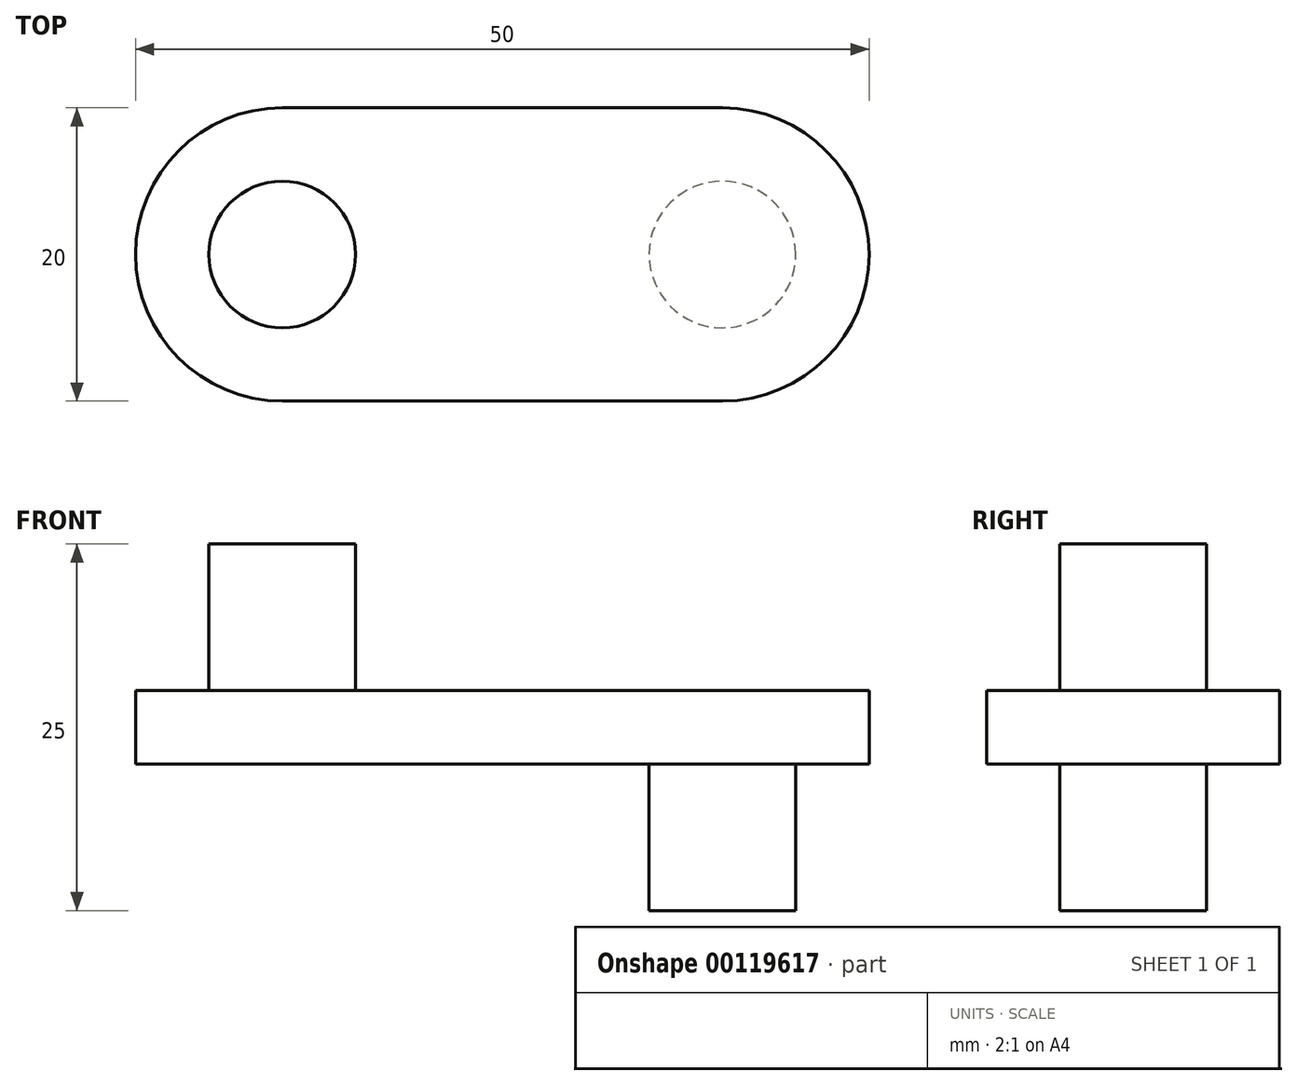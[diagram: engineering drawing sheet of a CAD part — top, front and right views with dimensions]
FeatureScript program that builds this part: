
annotation { "Feature Type Name" : "Feature", "Feature Type Description" : "" }
export const myFeature = defineFeature(function(context is Context, id is Id, definition is map)
    precondition{}
    {
        {
            var Q0;
            Q0=qCreatedBy(makeId("Top.planeOp"),FACE);
            var sketch = newSketch(context, id + "F0", { "sketchPlane" : qUnion([Q0])});
            skArc(sketch, "E0", {"start": v(-15, 10) * mm, "mid": v(-25, 0) * mm, "end": v(-15, -10) * mm});
            skArc(sketch, "E1", {"start": v(15, -10) * mm, "mid": v(25, 0) * mm, "end": v(15, 10) * mm});
            skLineSegment(sketch, "E2", {"start": v(-15, 10) * mm, "end": v(15, 10) * mm});
            skLineSegment(sketch, "E3", {"start": v(-15, -10) * mm, "end": v(15, -10) * mm});
            skSolve(sketch);
        }
        {
            var Q0;
            Q0 = qSketchRegion(id + "F0", true);
            extrude(context, id + "F1", {"entities" : qUnion([Q0]), "depth" : 5 * mm});
        }
        {
            var Q0;
            Q0=makeQuery(id+"F1.opExtrude","CAP_FACE",FACE,{"disambiguationData":[OSD([sQuery(id+"F0.wireOp",EDGE,"E0"),sQuery(id+"F0.wireOp",EDGE,"E1"),sQuery(id+"F0.wireOp",EDGE,"E2"),sQuery(id+"F0.wireOp",EDGE,"E3")])],"isStart":false});
            var sketch = newSketch(context, id + "F2", { "sketchPlane" : qUnion([Q0])});
            skCircle(sketch, "E4", {"center": v(-15, 0) * mm, "radius": 5 * mm});
            skSolve(sketch);
        }
        {
            var Q0;
            Q0 = qSketchRegion(id + "F2", true);
            extrude(context, id + "F3", {"entities" : qUnion([Q0]), "operationType" : NewBodyOperationType.ADD, "depth" : 10 * mm});
        }
        {
            var Q0;
            Q0=makeQuery(id+"F1.opExtrude","CAP_FACE",FACE,{"disambiguationData":[OSD([sQuery(id+"F0.wireOp",EDGE,"E0"),sQuery(id+"F0.wireOp",EDGE,"E1"),sQuery(id+"F0.wireOp",EDGE,"E2"),sQuery(id+"F0.wireOp",EDGE,"E3")])],"isStart":true});
            var sketch = newSketch(context, id + "F4", { "sketchPlane" : qUnion([Q0])});
            skCircle(sketch, "E5", {"center": v(15, 0) * mm, "radius": 5 * mm});
            skSolve(sketch);
        }
        {
            var Q0;
            Q0 = qSketchRegion(id + "F4", true);
            extrude(context, id + "F5", {"entities" : qUnion([Q0]), "operationType" : NewBodyOperationType.ADD, "depth" : 10 * mm});
        }
    });
